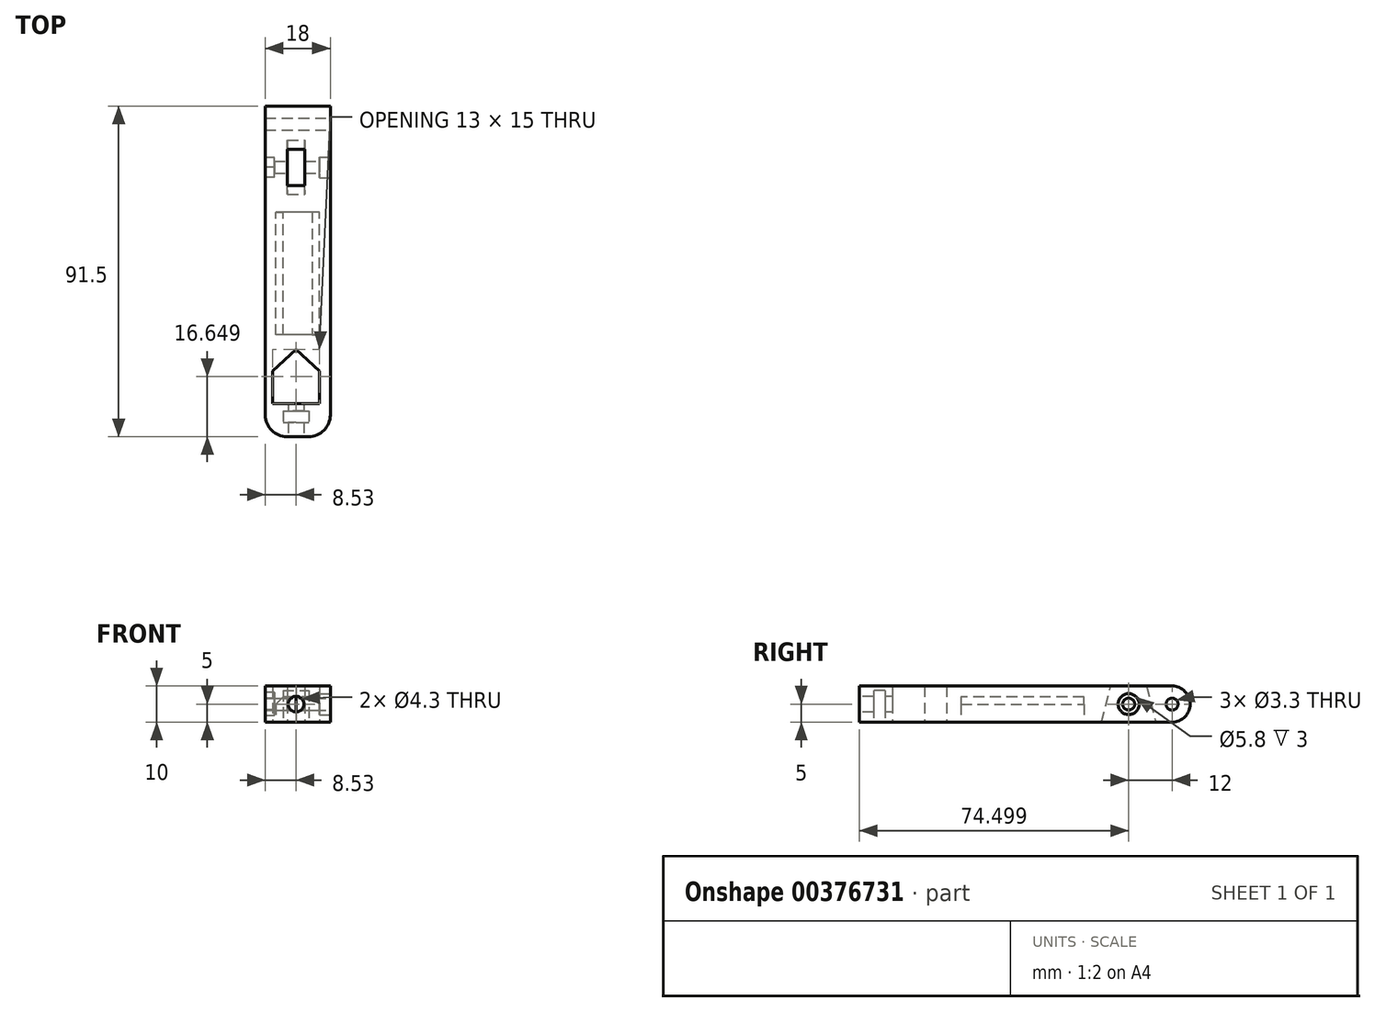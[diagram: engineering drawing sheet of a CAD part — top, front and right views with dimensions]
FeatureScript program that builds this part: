
annotation { "Feature Type Name" : "Feature", "Feature Type Description" : "" }
export const myFeature = defineFeature(function(context is Context, id is Id, definition is map)
    precondition{}
    {
        {
            var Q0;
            Q0=qCreatedBy(makeId("Top.planeOp"),FACE);
            var sketch = newSketch(context, id + "F0", { "sketchPlane" : qUnion([Q0])});
            skLineSegment(sketch, "E0.bottom", {"start": v(-8.53, 57.36) * mm, "end": v(9.47, 57.36) * mm});
            skLineSegment(sketch, "E0.top", {"start": v(-8.53, -34.14) * mm, "end": v(9.47, -34.14) * mm});
            skLineSegment(sketch, "E0.left", {"start": v(-8.53, 57.36) * mm, "end": v(-8.53, -34.14) * mm});
            skLineSegment(sketch, "E0.right", {"start": v(9.47, 57.36) * mm, "end": v(9.47, -34.14) * mm});
            skLineSegment(sketch, "E1.bottom", {"start": v(-3.6, -27) * mm, "end": v(3.6, -27) * mm});
            skLineSegment(sketch, "E1.top", {"start": v(-3.6, -30.14) * mm, "end": v(3.6, -30.14) * mm});
            skLineSegment(sketch, "E1.left", {"start": v(-3.6, -27) * mm, "end": v(-3.6, -30.14) * mm});
            skLineSegment(sketch, "E1.right", {"start": v(3.6, -27) * mm, "end": v(3.6, -30.14) * mm});
            skLineSegment(sketch, "E2", {"start": v(-6.5, -25) * mm, "end": v(6.5, -25) * mm});
            skLineSegment(sketch, "E3", {"start": v(6.5, -25) * mm, "end": v(6.5, -16) * mm});
            skLineSegment(sketch, "E4", {"start": v(6.5, -16) * mm, "end": v(0, -10) * mm});
            skLineSegment(sketch, "E5", {"start": v(0, -10) * mm, "end": v(-6.5, -16) * mm});
            skLineSegment(sketch, "E6", {"start": v(-6.5, -16) * mm, "end": v(-6.5, -25) * mm});
            skLineSegment(sketch, "E7.bottom", {"start": v(6.47, -6) * mm, "end": v(-5.53, -6) * mm});
            skLineSegment(sketch, "E7.top", {"start": v(6.47, 28) * mm, "end": v(-5.53, 28) * mm});
            skLineSegment(sketch, "E7.left", {"start": v(6.47, -6) * mm, "end": v(6.47, 28) * mm});
            skLineSegment(sketch, "E7.right", {"start": v(-5.53, -6) * mm, "end": v(-5.53, 28) * mm});
            skSolve(sketch);
        }
        {
            var Q0;
            Q0=makeQuery(id+"F0.imprint","IMPRINT",FACE,{"disambiguationData":[TD([[makeQuery(id+"F0.imprint","IMPRINT",EDGE,{"derivedFrom":sQuery(id+"F0.wireOp",EDGE,"E0.bottom")}),-1.0]])]});
            var Q1;
            Q1=makeQuery(id+"F0.imprint","IMPRINT",FACE,{"disambiguationData":[TD([[makeQuery(id+"F0.imprint","IMPRINT",EDGE,{"derivedFrom":sQuery(id+"F0.wireOp",EDGE,"E7.bottom")}),-1.0]])]});
            extrude(context, id + "F1", {"entities" : qUnion([Q0, Q1]), "depth" : 10 * mm});
        }
        {
            var Q0;
            Q0=makeQuery(id+"F1.opExtrude","SWEPT_EDGE",EDGE,{"disambiguationData":[OSD([sQuery(id+"F0.wireOp",EDGE,"E0.top"),sQuery(id+"F0.wireOp",EDGE,"E0.right")])]});
            var Q1;
            Q1=makeQuery(id+"F1.opExtrude","SWEPT_EDGE",EDGE,{"disambiguationData":[OSD([sQuery(id+"F0.wireOp",EDGE,"E0.top"),sQuery(id+"F0.wireOp",EDGE,"E0.left")])]});
            fillet(context, id + "F2", {"entities" : qUnion([Q0, Q1]), "radius" : 6 * mm, "tangentPropagation" : true, "allowEdgeOverflow" : false});
        }
        {
            var Q0;
            Q0=makeQuery(id+"F1.opExtrude","SWEPT_FACE",FACE,{"disambiguationData":[OSD([sQuery(id+"F0.wireOp",EDGE,"E0.right")])]});
            cPlane(context, id + "F3", {"entities" : qUnion([Q0]), "cplaneType" : CPlaneType.OFFSET, "offset" : 0 * mm, "width" : 150 * mm, "height" : 150 * mm});
        }
        {
            var Q0;
            Q0=makeQuery(id+"F0.imprint","IMPRINT",FACE,{"disambiguationData":[TD([[makeQuery(id+"F0.imprint","IMPRINT",EDGE,{"derivedFrom":sQuery(id+"F0.wireOp",EDGE,"E7.bottom")}),-1.0]])]});
            extrude(context, id + "F4", {"entities" : qUnion([Q0]), "operationType" : NewBodyOperationType.REMOVE, "depth" : 7 * mm});
        }
        {
            var Q0;
            Q0=makeQuery(id+"F4.boolean.opBoolean","COPY",EDGE,{"derivedFrom":makeQuery(id+"F4.opExtrude","CAP_EDGE",EDGE,{"disambiguationData":[OSD([sQuery(id+"F0.wireOp",EDGE,"E7.left")])],"isStart":false})});
            var Q1;
            Q1=makeQuery(id+"F4.boolean.opBoolean","COPY",EDGE,{"derivedFrom":makeQuery(id+"F4.opExtrude","CAP_EDGE",EDGE,{"disambiguationData":[OSD([sQuery(id+"F0.wireOp",EDGE,"E7.right")])],"isStart":false})});
            chamfer(context, id + "F5", {"entities" : qUnion([Q0, Q1]), "width" : 2 * mm, "tangentPropagation" : true});
        }
        {
            var Q0;
            Q0=qCreatedBy(id+"F3.planeOp",FACE);
            var sketch = newSketch(context, id + "F6", { "sketchPlane" : qUnion([Q0])});
            skLineSegment(sketch, "E8.0", {"start": v(57.36, 10) * mm, "end": v(-28.14, 10) * mm});
            skLineSegment(sketch, "E9.0", {"start": v(57.36, 0) * mm, "end": v(-28.14, 0) * mm});
            skLineSegment(sketch, "E10.0", {"start": v(57.36, 10) * mm, "end": v(57.36, 0) * mm});
            skLineSegment(sketch, "E11", {"start": v(40.36, 0) * mm, "end": v(40.36, 10) * mm});
            skCircle(sketch, "E12", {"center": v(40.36, 5) * mm, "radius": 1.65 * mm});
            skCircle(sketch, "E13", {"center": v(52.36, 5) * mm, "radius": 1.65 * mm});
            skCircle(sketch, "E14", {"center": v(40.36, 5) * mm, "radius": 2.9 * mm});
            skSolve(sketch);
        }
        {
            var Q0;
            {var subQ0=sQuery(id+"F6.wireOp",EDGE,"E12");var subQ1=sQuery(id+"F6.wireOp",EDGE,"E11");var subQ2=makeQuery(id+"F6.imprint","INTERSECT",VERTEX,{"disambiguationData":[OD(0.0)],"derivedFrom":[subQ1,subQ0]});Q0=makeQuery(id+"F6.imprint","IMPRINT",FACE,{"disambiguationData":[TD([[makeQuery(id+"F6.imprint","IMPRINT",EDGE,{"disambiguationData":[TD([[subQ2,-1.0]])],"derivedFrom":subQ1}),1.0]])]});}
            var Q1;
            {var subQ0=sQuery(id+"F6.wireOp",EDGE,"E12");var subQ1=sQuery(id+"F6.wireOp",EDGE,"E11");var subQ2=makeQuery(id+"F6.imprint","INTERSECT",VERTEX,{"disambiguationData":[OD(0.0)],"derivedFrom":[subQ1,subQ0]});Q1=makeQuery(id+"F6.imprint","IMPRINT",FACE,{"disambiguationData":[TD([[makeQuery(id+"F6.imprint","IMPRINT",EDGE,{"disambiguationData":[TD([[subQ2,-1.0]])],"derivedFrom":subQ1}),-1.0]])]});}
            var Q2;
            Q2=makeQuery(id+"F6.imprint","IMPRINT",FACE,{"disambiguationData":[TD([[makeQuery(id+"F6.imprint","IMPRINT",EDGE,{"derivedFrom":sQuery(id+"F6.wireOp",EDGE,"E13")}),1.0]])]});
            extrude(context, id + "F7", {"entities" : qUnion([Q0, Q1, Q2]), "operationType" : NewBodyOperationType.REMOVE, "oppositeDirection" : true, "depth" : 25 * mm});
        }
        {
            var Q0;
            {var subQ0=sQuery(id+"F6.wireOp",EDGE,"E14");var subQ1=sQuery(id+"F6.wireOp",EDGE,"E11");var subQ2=makeQuery(id+"F6.imprint","INTERSECT",VERTEX,{"disambiguationData":[OD(0.0)],"derivedFrom":[subQ1,subQ0]});Q0=makeQuery(id+"F6.imprint","IMPRINT",FACE,{"disambiguationData":[TD([[makeQuery(id+"F6.imprint","IMPRINT",EDGE,{"disambiguationData":[TD([[subQ2,-1.0]])],"derivedFrom":subQ1}),1.0]])]});}
            var Q1;
            {var subQ0=sQuery(id+"F6.wireOp",EDGE,"E14");var subQ1=sQuery(id+"F6.wireOp",EDGE,"E11");var subQ2=makeQuery(id+"F6.imprint","INTERSECT",VERTEX,{"disambiguationData":[OD(0.0)],"derivedFrom":[subQ1,subQ0]});Q1=makeQuery(id+"F6.imprint","IMPRINT",FACE,{"disambiguationData":[TD([[makeQuery(id+"F6.imprint","IMPRINT",EDGE,{"disambiguationData":[TD([[subQ2,-1.0]])],"derivedFrom":subQ1}),-1.0]])]});}
            extrude(context, id + "F8", {"entities" : qUnion([Q0, Q1]), "operationType" : NewBodyOperationType.REMOVE, "oppositeDirection" : true, "depth" : 3 * mm});
        }
        {
            var Q0;
            Q0=qCreatedBy(makeId("Right.planeOp"),FACE);
            cPlane(context, id + "F9", {"entities" : qUnion([Q0]), "cplaneType" : CPlaneType.OFFSET, "offset" : 0 * mm, "width" : 150 * mm, "height" : 150 * mm});
        }
        {
            var Q0;
            Q0=makeQuery(id+"F1.opExtrude","CAP_EDGE",EDGE,{"disambiguationData":[OSD([sQuery(id+"F0.wireOp",EDGE,"E0.bottom")])],"isStart":true});
            var Q1;
            Q1=makeQuery(id+"F1.opExtrude","CAP_EDGE",EDGE,{"disambiguationData":[OSD([sQuery(id+"F0.wireOp",EDGE,"E0.bottom")])],"isStart":false});
            fillet(context, id + "F10", {"entities" : qUnion([Q0, Q1]), "radius" : 5 * mm, "tangentPropagation" : true, "allowEdgeOverflow" : false});
        }
        {
            var Q0;
            Q0=qCreatedBy(id+"F9.planeOp",FACE);
            var sketch = newSketch(context, id + "F11", { "sketchPlane" : qUnion([Q0])});
            skLineSegment(sketch, "E15.0", {"start": v(67.94, 10) * mm, "end": v(-28.14, 10) * mm});
            skLineSegment(sketch, "E16.0", {"start": v(67.94, 0) * mm, "end": v(-28.14, 0) * mm});
            skLineSegment(sketch, "E17.0", {"start": v(67.94, 10) * mm, "end": v(67.94, 0) * mm});
            skLineSegment(sketch, "E18", {"start": v(32.86, 0) * mm, "end": v(35.36, 10) * mm});
            skLineSegment(sketch, "E19", {"start": v(35.36, 10) * mm, "end": v(45.36, 10) * mm});
            skLineSegment(sketch, "E20", {"start": v(45.36, 10) * mm, "end": v(47.86, 0) * mm});
            skLineSegment(sketch, "E21", {"start": v(47.86, 0) * mm, "end": v(32.86, 0) * mm});
            skLineSegment(sketch, "E22", {"start": v(32.86, 0) * mm, "end": v(47.86, 0) * mm});
            skPoint(sketch, "E23.0", {"position": v(40.36, 5) * mm});
            skSolve(sketch);
        }
        {
            var Q0;
            Q0=makeQuery(id+"F11.imprint","IMPRINT",FACE,{"disambiguationData":[TD([[makeQuery(id+"F11.imprint","IMPRINT",EDGE,{"derivedFrom":sQuery(id+"F11.wireOp",EDGE,"E18")}),-1.0]])]});
            extrude(context, id + "F12", {"entities" : qUnion([Q0]), "operationType" : NewBodyOperationType.REMOVE, "endBound" : BoundingType.SYMMETRIC, "oppositeDirection" : true, "depth" : 4.8 * mm});
        }
        {
            var Q0;
            Q0=makeQuery(id+"F1.opExtrude","SWEPT_FACE",FACE,{"disambiguationData":[OSD([sQuery(id+"F0.wireOp",EDGE,"E0.left")])]});
            cPlane(context, id + "F13", {"entities" : qUnion([Q0]), "cplaneType" : CPlaneType.OFFSET, "offset" : 0 * mm, "width" : 150 * mm, "height" : 150 * mm});
        }
        {
            var Q0;
            Q0=qCreatedBy(id+"F13.planeOp",FACE);
            var sketch = newSketch(context, id + "F14", { "sketchPlane" : qUnion([Q0])});
            skPoint(sketch, "E24.0", {"position": v(-40.36, 5) * mm});
            skCircle(sketch, "E25", {"center": v(-40.36, 5) * mm, "radius": 3.2 * mm});
            skCircle(sketch, "E26.cCircle", {"center": v(-40.36, 5) * mm, "radius": 3.2 * mm, "construction": true});
            skLineSegment(sketch, "E26.0", {"start": v(-40.36, 1.8) * mm, "end": v(-43.13, 3.4) * mm});
            skLineSegment(sketch, "E26.1", {"start": v(-43.13, 3.4) * mm, "end": v(-43.13, 6.6) * mm});
            skLineSegment(sketch, "E26.2", {"start": v(-43.13, 6.6) * mm, "end": v(-40.36, 8.2) * mm});
            skLineSegment(sketch, "E26.3", {"start": v(-40.36, 8.2) * mm, "end": v(-37.59, 6.6) * mm});
            skLineSegment(sketch, "E26.4", {"start": v(-37.59, 6.6) * mm, "end": v(-37.59, 3.4) * mm});
            skLineSegment(sketch, "E26.5", {"start": v(-37.59, 3.4) * mm, "end": v(-40.36, 1.8) * mm});
            skSolve(sketch);
        }
        {
            var Q0;
            Q0=makeQuery(id+"F14.imprint","IMPRINT",FACE,{"disambiguationData":[TD([[makeQuery(id+"F14.imprint","IMPRINT",EDGE,{"derivedFrom":sQuery(id+"F14.wireOp",EDGE,"E26.0")}),-1.0]])]});
            extrude(context, id + "F15", {"entities" : qUnion([Q0]), "operationType" : NewBodyOperationType.REMOVE, "oppositeDirection" : true, "depth" : 2.5 * mm});
        }
        {
            var Q0;
            Q0=makeQuery(id+"F1.opExtrude","SWEPT_FACE",FACE,{"disambiguationData":[OSD([sQuery(id+"F0.wireOp",EDGE,"E0.top")])]});
            cPlane(context, id + "F16", {"entities" : qUnion([Q0]), "cplaneType" : CPlaneType.OFFSET, "offset" : 0 * mm, "width" : 150 * mm, "height" : 150 * mm});
        }
        {
            var Q0;
            Q0=qCreatedBy(id+"F16.planeOp",FACE);
            var sketch = newSketch(context, id + "F17", { "sketchPlane" : qUnion([Q0])});
            skCircle(sketch, "E27", {"center": v(0, 5) * mm, "radius": 2.15 * mm});
            skSolve(sketch);
        }
        {
            var Q0;
            Q0=makeQuery(id+"F17.imprint","IMPRINT",FACE,{"disambiguationData":[TD([[makeQuery(id+"F17.imprint","IMPRINT",EDGE,{"derivedFrom":sQuery(id+"F17.wireOp",EDGE,"E27")}),1.0]])]});
            extrude(context, id + "F18", {"entities" : qUnion([Q0]), "operationType" : NewBodyOperationType.REMOVE, "oppositeDirection" : true, "depth" : 20 * mm});
        }
        {
            var Q0;
            Q0=makeQuery(id+"F1.opExtrude","CAP_FACE",FACE,{"disambiguationData":[OSD([sQuery(id+"F0.wireOp",EDGE,"E0.bottom"),sQuery(id+"F0.wireOp",EDGE,"E0.top"),sQuery(id+"F0.wireOp",EDGE,"E0.left"),sQuery(id+"F0.wireOp",EDGE,"E0.right"),sQuery(id+"F0.wireOp",EDGE,"E1.bottom"),sQuery(id+"F0.wireOp",EDGE,"E1.top"),sQuery(id+"F0.wireOp",EDGE,"E1.left"),sQuery(id+"F0.wireOp",EDGE,"E1.right"),sQuery(id+"F0.wireOp",EDGE,"E2"),sQuery(id+"F0.wireOp",EDGE,"E3"),sQuery(id+"F0.wireOp",EDGE,"E4"),sQuery(id+"F0.wireOp",EDGE,"E5"),sQuery(id+"F0.wireOp",EDGE,"E6")])],"isStart":false});
            cPlane(context, id + "F19", {"entities" : qUnion([Q0]), "cplaneType" : CPlaneType.OFFSET, "offset" : 0 * mm, "width" : 150 * mm, "height" : 150 * mm});
        }
        {
            var Q0;
            Q0=qCreatedBy(id+"F19.planeOp",FACE);
            var sketch = newSketch(context, id + "F20", { "sketchPlane" : qUnion([Q0])});
            skLineSegment(sketch, "E28.0", {"start": v(-3.6, -27) * mm, "end": v(3.6, -27) * mm});
            skLineSegment(sketch, "E29.0", {"start": v(-3.6, -30.14) * mm, "end": v(3.6, -30.14) * mm});
            skLineSegment(sketch, "E30.0", {"start": v(3.6, -27) * mm, "end": v(3.6, -30.14) * mm});
            skLineSegment(sketch, "E31.0", {"start": v(-3.6, -27) * mm, "end": v(-3.6, -30.14) * mm});
            skSolve(sketch);
        }
        {
            var Q0;
            Q0 = qSketchRegion(id + "F20", true);
            extrude(context, id + "F21", {"entities" : qUnion([Q0]), "operationType" : NewBodyOperationType.ADD, "oppositeDirection" : true, "depth" : 1.25 * mm});
        }
    });
